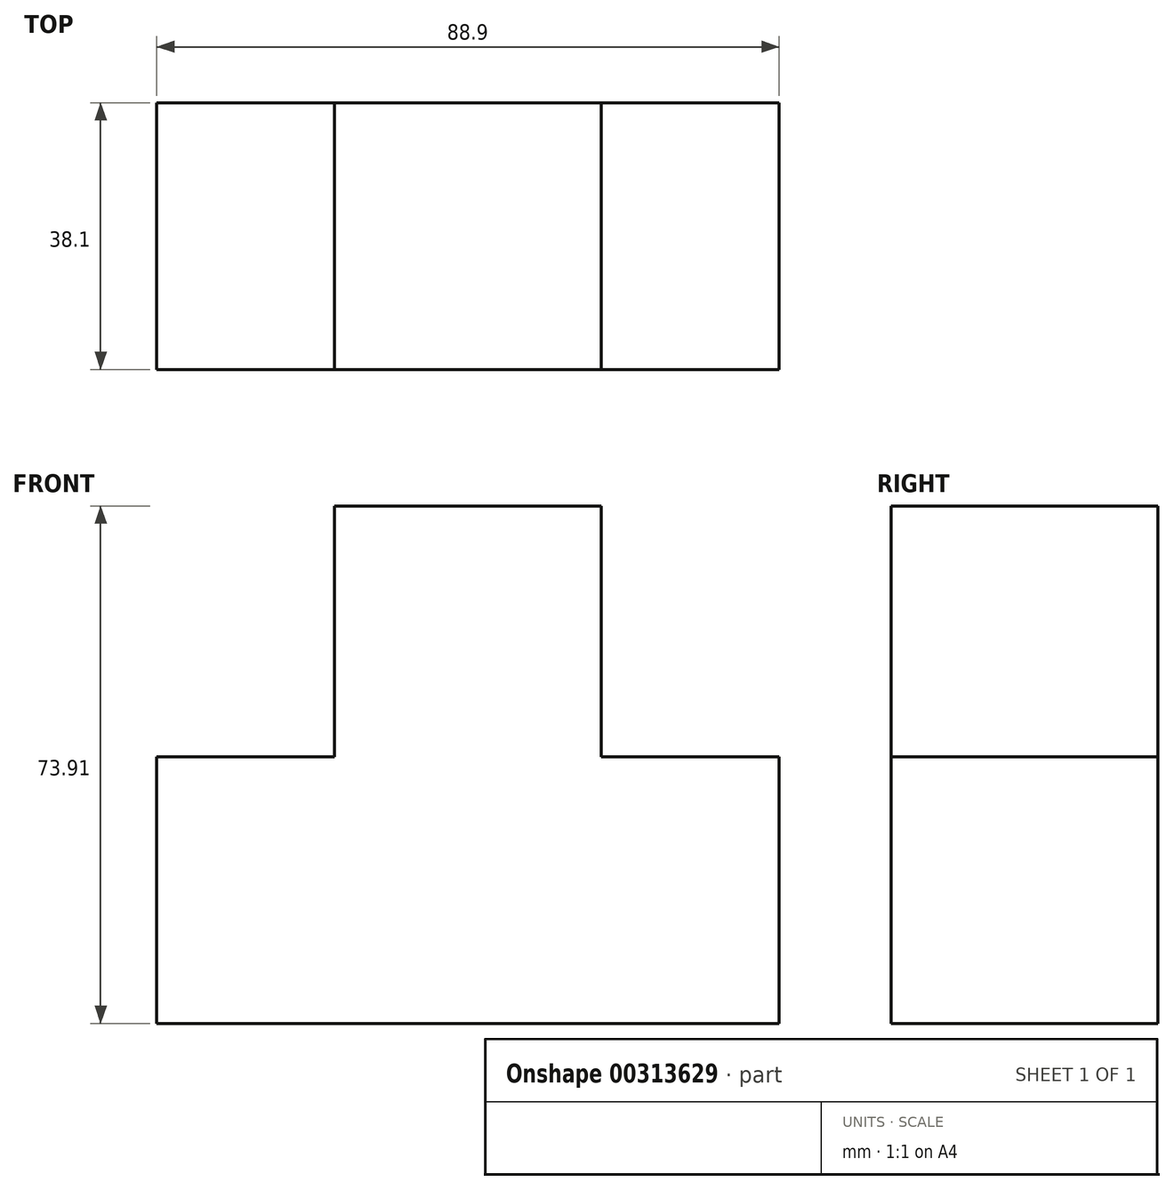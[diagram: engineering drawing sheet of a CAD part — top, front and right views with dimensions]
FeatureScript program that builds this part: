
annotation { "Feature Type Name" : "Feature", "Feature Type Description" : "" }
export const myFeature = defineFeature(function(context is Context, id is Id, definition is map)
    precondition{}
    {
        {
            var Q0;
            Q0=qCreatedBy(makeId("Front.planeOp"),FACE);
            var sketch = newSketch(context, id + "F0", { "sketchPlane" : qUnion([Q0])});
            skLineSegment(sketch, "E0", {"start": v(-37, -60.58) * mm, "end": v(51.9, -60.58) * mm});
            skLineSegment(sketch, "E1", {"start": v(51.9, -60.58) * mm, "end": v(51.9, -22.48) * mm});
            skLineSegment(sketch, "E2", {"start": v(51.9, -22.48) * mm, "end": v(26.5, -22.48) * mm});
            skLineSegment(sketch, "E3", {"start": v(26.5, -22.48) * mm, "end": v(26.5, 13.33) * mm});
            skLineSegment(sketch, "E4", {"start": v(26.5, 13.33) * mm, "end": v(-11.6, 13.33) * mm});
            skLineSegment(sketch, "E5", {"start": v(-11.6, 13.33) * mm, "end": v(-11.6, -22.48) * mm});
            skLineSegment(sketch, "E6", {"start": v(-11.6, -22.48) * mm, "end": v(-37, -22.48) * mm});
            skLineSegment(sketch, "E7", {"start": v(-37, -22.48) * mm, "end": v(-37, -60.58) * mm});
            skSolve(sketch);
        }
        {
            var Q0;
            Q0=makeQuery(id+"F0.imprint","IMPRINT",FACE,{"disambiguationData":[TD([[makeQuery(id+"F0.imprint","IMPRINT",EDGE,{"derivedFrom":sQuery(id+"F0.wireOp",EDGE,"E0")}),1.0]])]});
            extrude(context, id + "F1", {"entities" : qUnion([Q0]), "depth" : 38.1 * mm});
        }
    });
